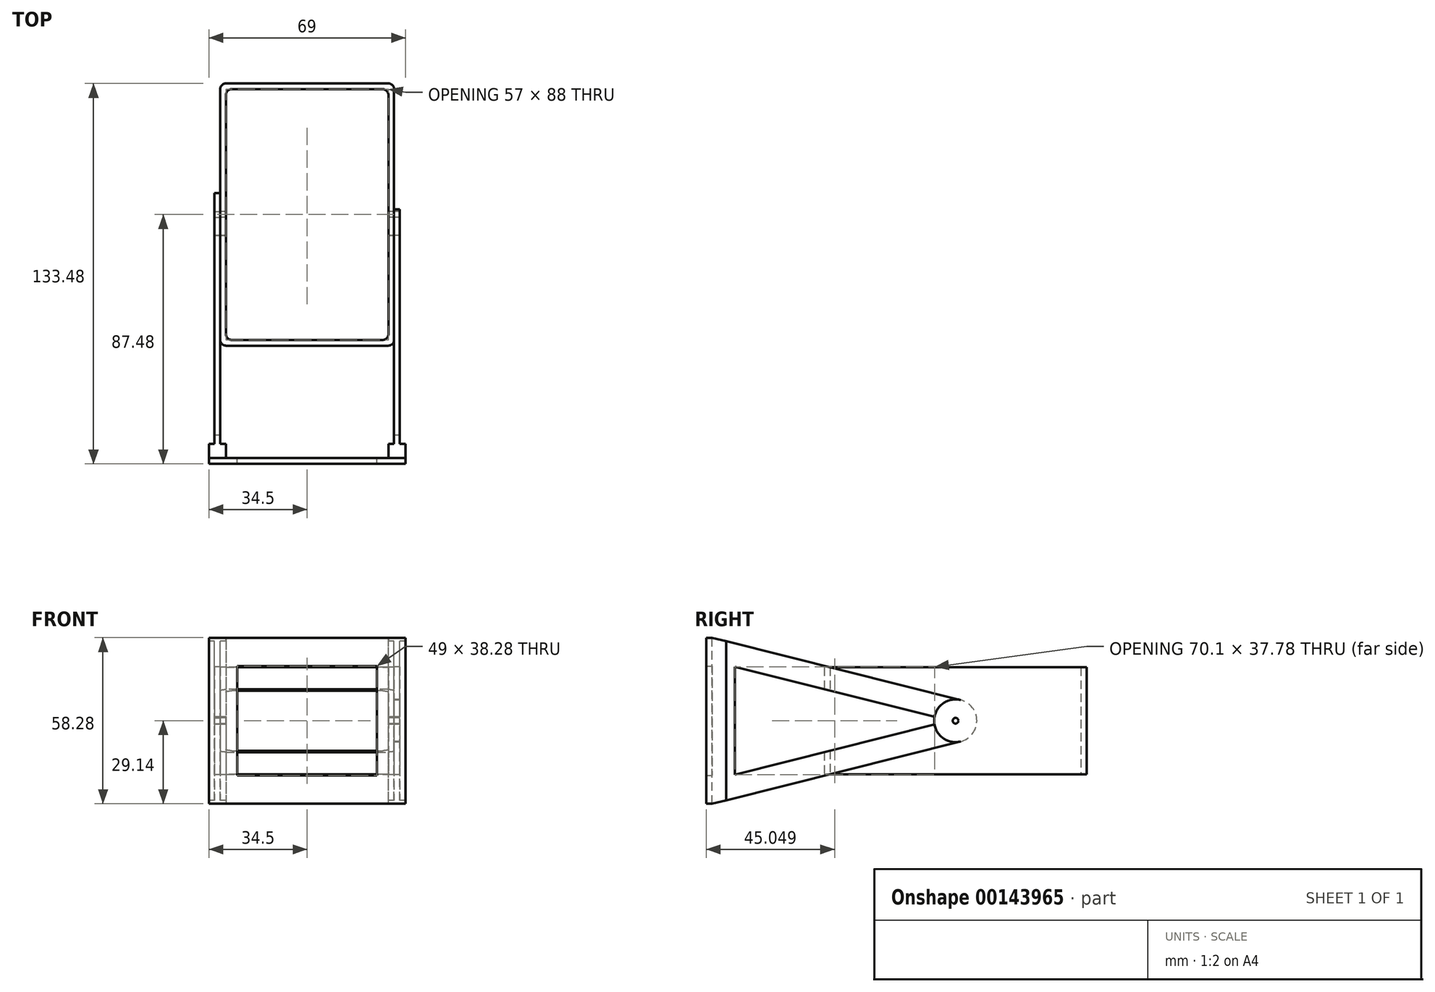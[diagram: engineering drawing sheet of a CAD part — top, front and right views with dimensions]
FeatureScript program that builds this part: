
annotation { "Feature Type Name" : "Feature", "Feature Type Description" : "" }
export const myFeature = defineFeature(function(context is Context, id is Id, definition is map)
    precondition{}
    {
        {
            var Q0;
            Q0=qCreatedBy(makeId("Top.planeOp"),FACE);
            var sketch = newSketch(context, id + "F0", { "sketchPlane" : qUnion([Q0])});
            skLineSegment(sketch, "E0", {"start": v(-28.5, 0) * mm, "end": v(-28.5, 42) * mm});
            skLineSegment(sketch, "E1", {"start": v(-26.5, 44) * mm, "end": v(26.5, 44) * mm});
            skLineSegment(sketch, "E2", {"start": v(28.5, 42) * mm, "end": v(28.5, 0) * mm});
            skLineSegment(sketch, "E3", {"start": v(28.5, 0) * mm, "end": v(28.5, -42) * mm});
            skLineSegment(sketch, "E4", {"start": v(26.5, -44) * mm, "end": v(-26.5, -44) * mm});
            skLineSegment(sketch, "E5", {"start": v(-28.5, -42) * mm, "end": v(-28.5, 0) * mm});
            skLineSegment(sketch, "E6", {"start": v(0, 0) * mm, "end": v(28.5, 0) * mm, "construction": true});
            skLineSegment(sketch, "E7", {"start": v(0, 0) * mm, "end": v(-28.5, 0) * mm, "construction": true});
            skPoint(sketch, "E8.visualSharp", {"position": v(-28.5, 44) * mm});
            skArc(sketch, "E8.filletArc", {"start": v(-26.5, 44) * mm, "mid": v(-27.91, 43.41) * mm, "end": v(-28.5, 42) * mm});
            skPoint(sketch, "E9.visualSharp", {"position": v(28.5, 44) * mm});
            skArc(sketch, "E9.filletArc", {"start": v(28.5, 42) * mm, "mid": v(27.91, 43.41) * mm, "end": v(26.5, 44) * mm});
            skPoint(sketch, "E10.visualSharp", {"position": v(28.5, -44) * mm});
            skArc(sketch, "E10.filletArc", {"start": v(26.5, -44) * mm, "mid": v(27.91, -43.41) * mm, "end": v(28.5, -42) * mm});
            skPoint(sketch, "E11.visualSharp", {"position": v(-28.5, -44) * mm});
            skArc(sketch, "E11.filletArc", {"start": v(-28.5, -42) * mm, "mid": v(-27.91, -43.41) * mm, "end": v(-26.5, -44) * mm});
            skLineSegment(sketch, "E12", {"start": v(-30.5, 0) * mm, "end": v(-30.5, 44) * mm});
            skLineSegment(sketch, "E13", {"start": v(-28.5, 46) * mm, "end": v(28.5, 46) * mm});
            skLineSegment(sketch, "E14", {"start": v(30.5, 44) * mm, "end": v(30.5, 0) * mm});
            skLineSegment(sketch, "E15", {"start": v(30.5, 0) * mm, "end": v(30.5, -44) * mm});
            skLineSegment(sketch, "E16", {"start": v(28.5, -46) * mm, "end": v(-28.5, -46) * mm});
            skLineSegment(sketch, "E17", {"start": v(-30.5, -44) * mm, "end": v(-30.5, 0) * mm});
            skPoint(sketch, "E18.visualSharp", {"position": v(-30.5, 46) * mm});
            skArc(sketch, "E18.filletArc", {"start": v(-28.5, 46) * mm, "mid": v(-29.91, 45.41) * mm, "end": v(-30.5, 44) * mm});
            skPoint(sketch, "E19.visualSharp", {"position": v(30.5, 46) * mm});
            skArc(sketch, "E19.filletArc", {"start": v(30.5, 44) * mm, "mid": v(29.91, 45.41) * mm, "end": v(28.5, 46) * mm});
            skPoint(sketch, "E20.visualSharp", {"position": v(30.5, -46) * mm});
            skArc(sketch, "E20.filletArc", {"start": v(28.5, -46) * mm, "mid": v(29.91, -45.41) * mm, "end": v(30.5, -44) * mm});
            skPoint(sketch, "E21.visualSharp", {"position": v(-30.5, -46) * mm});
            skArc(sketch, "E21.filletArc", {"start": v(-30.5, -44) * mm, "mid": v(-29.91, -45.41) * mm, "end": v(-28.5, -46) * mm});
            skLineSegment(sketch, "E22", {"start": v(0, 0) * mm, "end": v(0, -46) * mm, "construction": true});
            skLineSegment(sketch, "E23", {"start": v(10, -44) * mm, "end": v(10, -29) * mm});
            skLineSegment(sketch, "E24", {"start": v(-10, -29) * mm, "end": v(-10, -44) * mm});
            skLineSegment(sketch, "E25", {"start": v(-8, -27) * mm, "end": v(0, -27) * mm});
            skLineSegment(sketch, "E26", {"start": v(0, -27) * mm, "end": v(8, -27) * mm});
            skPoint(sketch, "E27.visualSharp", {"position": v(10, -27) * mm});
            skArc(sketch, "E27.filletArc", {"start": v(10, -29) * mm, "mid": v(9.41, -27.59) * mm, "end": v(8, -27) * mm});
            skPoint(sketch, "E28.visualSharp", {"position": v(-10, -27) * mm});
            skArc(sketch, "E28.filletArc", {"start": v(-8, -27) * mm, "mid": v(-9.41, -27.59) * mm, "end": v(-10, -29) * mm});
            skLineSegment(sketch, "E29", {"start": v(9.5, -44) * mm, "end": v(9.5, -41) * mm});
            skLineSegment(sketch, "E30", {"start": v(9.2, -40.7) * mm, "end": v(0, -40.7) * mm});
            skLineSegment(sketch, "E31", {"start": v(0, -40.7) * mm, "end": v(-5.2, -40.7) * mm});
            skLineSegment(sketch, "E32", {"start": v(-5.5, -41) * mm, "end": v(-5.5, -44) * mm});
            skPoint(sketch, "E33.visualSharp", {"position": v(9.5, -40.7) * mm});
            skArc(sketch, "E33.filletArc", {"start": v(9.5, -41) * mm, "mid": v(9.41, -40.79) * mm, "end": v(9.2, -40.7) * mm});
            skPoint(sketch, "E34.visualSharp", {"position": v(-5.5, -40.7) * mm});
            skArc(sketch, "E34.filletArc", {"start": v(-5.2, -40.7) * mm, "mid": v(-5.41, -40.79) * mm, "end": v(-5.5, -41) * mm});
            skPoint(sketch, "E35.cornerSnap0", {"position": v(-29.91, -45.41) * mm});
            skSolve(sketch);
        }
        {
            var Q0;
            Q0=makeQuery(id+"F0.imprint","IMPRINT",FACE,{"disambiguationData":[TD([[makeQuery(id+"F0.imprint","IMPRINT",EDGE,{"derivedFrom":sQuery(id+"F0.wireOp",EDGE,"E0")}),1.0]])]});
            extrude(context, id + "F1", {"entities" : qUnion([Q0]), "depth" : 35 * mm, "hasSecondDirection" : true, "secondDirectionOppositeDirection" : true, "secondDirectionDepth" : 2.5 * mm});
        }
        {
            var Q0;
            Q0=makeQuery(id+"F1.opExtrude","SWEPT_FACE",FACE,{"disambiguationData":[OSD([sQuery(id+"F0.wireOp",EDGE,"E12"),sQuery(id+"F0.wireOp",EDGE,"E17")])]});
            var sketch = newSketch(context, id + "F2", { "sketchPlane" : qUnion([Q0])});
            skCircle(sketch, "E36", {"center": v(0, 16.25) * mm, "radius": 1 * mm});
            skLineSegment(sketch, "E37.0", {"start": v(-44, 35) * mm, "end": v(-44, -2.5) * mm});
            skLineSegment(sketch, "E38.0", {"start": v(44, 35) * mm, "end": v(44, -2.5) * mm});
            skLineSegment(sketch, "E39", {"start": v(44, -2.5) * mm, "end": v(-44, 35) * mm, "construction": true});
            skLineSegment(sketch, "E40", {"start": v(-44, -2.5) * mm, "end": v(44, 35) * mm, "construction": true});
            skSolve(sketch);
        }
        {
            var Q0;
            Q0=makeQuery(id+"F2.imprint","IMPRINT",FACE,{"disambiguationData":[TD([[makeQuery(id+"F2.imprint","IMPRINT",EDGE,{"derivedFrom":sQuery(id+"F2.wireOp",EDGE,"E36")}),1.0]])]});
            extrude(context, id + "F3", {"entities" : qUnion([Q0]), "operationType" : NewBodyOperationType.REMOVE, "endBound" : BoundingType.THROUGH_ALL, "oppositeDirection" : true, "depth" : 25 * mm});
        }
        {
            var Q0;
            Q0=makeQuery(id+"F1.opExtrude","SWEPT_FACE",FACE,{"disambiguationData":[OSD([sQuery(id+"F0.wireOp",EDGE,"E12"),sQuery(id+"F0.wireOp",EDGE,"E17")])]});
            cPlane(context, id + "F4", {"entities" : qUnion([Q0]), "cplaneType" : CPlaneType.OFFSET, "offset" : 0 * mm, "width" : 150 * mm, "height" : 150 * mm});
        }
        {
            var Q0;
            Q0=qCreatedBy(id+"F4.planeOp",FACE);
            var sketch = newSketch(context, id + "F5", { "sketchPlane" : qUnion([Q0])});
            skCircle(sketch, "E41.0", {"center": v(0, 16.25) * mm, "radius": 1 * mm});
            skCircle(sketch, "E42", {"center": v(0, 16.25) * mm, "radius": 7.5 * mm});
            skLineSegment(sketch, "E43.0", {"start": v(44, 35) * mm, "end": v(44, -2.5) * mm});
            skLineSegment(sketch, "E44", {"start": v(-1.82, 8.97) * mm, "end": v(85.48, -12.89) * mm});
            skLineSegment(sketch, "E45", {"start": v(-1.82, 23.53) * mm, "end": v(85.48, 45.39) * mm});
            skLineSegment(sketch, "E46", {"start": v(85.48, -12.89) * mm, "end": v(85.48, 45.39) * mm});
            skSolve(sketch);
        }
        {
            var Q0;
            {var subQ0=sQuery(id+"F5.wireOp",EDGE,"E43.0");Q0=makeQuery(id+"F5.imprint","IMPRINT",FACE,{"disambiguationData":[TD([[makeQuery(id+"F5.imprint","IMPRINT",EDGE,{"derivedFrom":subQ0}),1.0]])]});}
            var Q1;
            {var subQ5=sQuery(id+"F5.wireOp",EDGE,"E43.0");Q1=makeQuery(id+"F5.imprint","IMPRINT",FACE,{"disambiguationData":[TD([[makeQuery(id+"F5.imprint","IMPRINT",EDGE,{"derivedFrom":subQ5}),-1.0]])]});}
            var Q2;
            Q2=makeQuery(id+"F5.imprint","IMPRINT",FACE,{"disambiguationData":[TD([[makeQuery(id+"F5.imprint","IMPRINT",EDGE,{"derivedFrom":sQuery(id+"F5.wireOp",EDGE,"E41.0")}),-1.0]])]});
            extrude(context, id + "F6", {"entities" : qUnion([Q0, Q1, Q2]), "depth" : 2 * mm});
        }
        {
            var Q0;
            Q0=makeQuery(id+"F1.opExtrude","SWEPT_FACE",FACE,{"disambiguationData":[OSD([sQuery(id+"F0.wireOp",EDGE,"E14"),sQuery(id+"F0.wireOp",EDGE,"E15")])]});
            cPlane(context, id + "F7", {"entities" : qUnion([Q0]), "cplaneType" : CPlaneType.OFFSET, "offset" : 0 * mm, "width" : 150 * mm, "height" : 150 * mm});
        }
        {
            var Q0;
            Q0=qCreatedBy(id+"F7.planeOp",FACE);
            var sketch = newSketch(context, id + "F8", { "sketchPlane" : qUnion([Q0])});
            skLineSegment(sketch, "E47.0", {"start": v(1.82, 23.53) * mm, "end": v(-85.48, 45.39) * mm});
            skCircle(sketch, "E47.1", {"center": v(0, 16.25) * mm, "radius": 7.5 * mm});
            skCircle(sketch, "E47.2", {"center": v(0, 16.25) * mm, "radius": 1 * mm});
            skLineSegment(sketch, "E47.3", {"start": v(1.82, 8.97) * mm, "end": v(-85.48, -12.89) * mm});
            skLineSegment(sketch, "E47.4", {"start": v(-85.48, -12.89) * mm, "end": v(-85.48, 45.39) * mm});
            skSolve(sketch);
        }
        {
            var Q0;
            {var subQ0=sQuery(id+"F8.wireOp",EDGE,"E47.0");Q0=makeQuery(id+"F8.imprint","IMPRINT",FACE,{"disambiguationData":[TD([[makeQuery(id+"F8.imprint","IMPRINT",EDGE,{"derivedFrom":subQ0}),1.0]])]});}
            var Q1;
            Q1=makeQuery(id+"F8.imprint","IMPRINT",FACE,{"disambiguationData":[TD([[makeQuery(id+"F8.imprint","IMPRINT",EDGE,{"derivedFrom":sQuery(id+"F8.wireOp",EDGE,"E47.2")}),1.0]])]});
            extrude(context, id + "F9", {"entities" : qUnion([Q0, Q1]), "depth" : 2 * mm});
        }
        {
            var Q0;
            Q0=makeQuery(id+"F6.opExtrude","SWEPT_FACE",FACE,{"disambiguationData":[OSD([sQuery(id+"F5.wireOp",EDGE,"E46")])]});
            var sketch = newSketch(context, id + "F10", { "sketchPlane" : qUnion([Q0])});
            skLineSegment(sketch, "E48.0", {"start": v(32.5, -12.89) * mm, "end": v(32.5, 45.39) * mm});
            skLineSegment(sketch, "E48.1", {"start": v(30.5, -12.89) * mm, "end": v(30.5, 45.39) * mm});
            skLineSegment(sketch, "E48.2", {"start": v(-30.5, -12.89) * mm, "end": v(-30.5, 45.39) * mm});
            skLineSegment(sketch, "E48.3", {"start": v(-32.5, -12.89) * mm, "end": v(-32.5, 45.39) * mm});
            skLineSegment(sketch, "E49", {"start": v(34.5, -12.89) * mm, "end": v(-34.5, -12.89) * mm});
            skPoint(sketch, "E49.endSnap0", {"position": v(-31.5, -12.89) * mm});
            skLineSegment(sketch, "E50", {"start": v(-34.5, -12.89) * mm, "end": v(-34.5, 45.39) * mm});
            skLineSegment(sketch, "E51", {"start": v(-34.5, 45.39) * mm, "end": v(34.5, 45.39) * mm});
            skLineSegment(sketch, "E52", {"start": v(34.5, 45.39) * mm, "end": v(34.5, -12.89) * mm});
            skLineSegment(sketch, "E53", {"start": v(28.5, -12.89) * mm, "end": v(28.5, 45.39) * mm});
            skLineSegment(sketch, "E54", {"start": v(-28.5, 45.39) * mm, "end": v(-28.5, -12.89) * mm});
            skLineSegment(sketch, "E55.bottom", {"start": v(-24.5, 35.39) * mm, "end": v(24.5, 35.39) * mm});
            skLineSegment(sketch, "E55.top", {"start": v(-24.5, -2.89) * mm, "end": v(24.5, -2.89) * mm});
            skLineSegment(sketch, "E55.left", {"start": v(-24.5, 35.39) * mm, "end": v(-24.5, -2.89) * mm});
            skLineSegment(sketch, "E55.right", {"start": v(24.5, 35.39) * mm, "end": v(24.5, -2.89) * mm});
            skSolve(sketch);
        }
        {
            var Q0;
            {var subQ0=sQuery(id+"F10.wireOp",EDGE,"E48.0");Q0=makeQuery(id+"F10.imprint","IMPRINT",FACE,{"disambiguationData":[TD([[makeQuery(id+"F10.imprint","IMPRINT",EDGE,{"derivedFrom":subQ0}),-1.0]])]});}
            var Q1;
            {var subQ0=sQuery(id+"F10.wireOp",EDGE,"E48.1");Q1=makeQuery(id+"F10.imprint","IMPRINT",FACE,{"disambiguationData":[TD([[makeQuery(id+"F10.imprint","IMPRINT",EDGE,{"derivedFrom":subQ0}),1.0]])]});}
            var Q2;
            {var subQ0=sQuery(id+"F10.wireOp",EDGE,"E48.2");Q2=makeQuery(id+"F10.imprint","IMPRINT",FACE,{"disambiguationData":[TD([[makeQuery(id+"F10.imprint","IMPRINT",EDGE,{"derivedFrom":subQ0}),-1.0]])]});}
            var Q3;
            {var subQ0=sQuery(id+"F10.wireOp",EDGE,"E48.3");Q3=makeQuery(id+"F10.imprint","IMPRINT",FACE,{"disambiguationData":[TD([[makeQuery(id+"F10.imprint","IMPRINT",EDGE,{"derivedFrom":subQ0}),1.0]])]});}
            extrude(context, id + "F11", {"entities" : qUnion([Q0, Q1, Q2, Q3]), "oppositeDirection" : true, "depth" : 5 * mm});
        }
        {
            var Q0;
            {var subQ0=sQuery(id+"F10.wireOp",EDGE,"E48.0");Q0=makeQuery(id+"F10.imprint","IMPRINT",FACE,{"disambiguationData":[TD([[makeQuery(id+"F10.imprint","IMPRINT",EDGE,{"derivedFrom":subQ0}),-1.0]])]});}
            var Q1;
            {var subQ0=sQuery(id+"F10.wireOp",EDGE,"E48.0");Q1=makeQuery(id+"F10.imprint","IMPRINT",FACE,{"disambiguationData":[TD([[makeQuery(id+"F10.imprint","IMPRINT",EDGE,{"derivedFrom":subQ0}),1.0]])]});}
            var Q2;
            {var subQ0=sQuery(id+"F10.wireOp",EDGE,"E53");Q2=makeQuery(id+"F10.imprint","IMPRINT",FACE,{"disambiguationData":[TD([[makeQuery(id+"F10.imprint","IMPRINT",EDGE,{"derivedFrom":subQ0}),1.0]])]});}
            var Q3;
            {var subQ0=sQuery(id+"F10.wireOp",EDGE,"E48.2");Q3=makeQuery(id+"F10.imprint","IMPRINT",FACE,{"disambiguationData":[TD([[makeQuery(id+"F10.imprint","IMPRINT",EDGE,{"derivedFrom":subQ0}),-1.0]])]});}
            var Q4;
            {var subQ0=sQuery(id+"F10.wireOp",EDGE,"E48.2");Q4=makeQuery(id+"F10.imprint","IMPRINT",FACE,{"disambiguationData":[TD([[makeQuery(id+"F10.imprint","IMPRINT",EDGE,{"derivedFrom":subQ0}),1.0]])]});}
            var Q5;
            {var subQ0=sQuery(id+"F10.wireOp",EDGE,"E48.3");Q5=makeQuery(id+"F10.imprint","IMPRINT",FACE,{"disambiguationData":[TD([[makeQuery(id+"F10.imprint","IMPRINT",EDGE,{"derivedFrom":subQ0}),1.0]])]});}
            var Q6;
            {var subQ0=sQuery(id+"F10.wireOp",EDGE,"E48.1");Q6=makeQuery(id+"F10.imprint","IMPRINT",FACE,{"disambiguationData":[TD([[makeQuery(id+"F10.imprint","IMPRINT",EDGE,{"derivedFrom":subQ0}),1.0]])]});}
            extrude(context, id + "F12", {"entities" : qUnion([Q0, Q1, Q2, Q3, Q4, Q5, Q6]), "operationType" : NewBodyOperationType.ADD, "depth" : 2 * mm});
        }
        {
            var Q0;
            {var subQ0=sQuery(id+"F10.wireOp",EDGE,"E50");Q0=makeQuery(id+"F12.boolean.opBoolean","MERGE",FACE,{"derivedFrom":[makeQuery(id+"F11.opExtrude","SWEPT_FACE",FACE,{"disambiguationData":[OSD([subQ0])]}),makeQuery(id+"F12.opExtrude","SWEPT_FACE",FACE,{"disambiguationData":[OSD([subQ0])]})]});}
            var sketch = newSketch(context, id + "F13", { "sketchPlane" : qUnion([Q0])});
            skLineSegment(sketch, "E56.0", {"start": v(-1.82, 23.53) * mm, "end": v(85.48, 45.39) * mm});
            skLineSegment(sketch, "E57.0", {"start": v(-1.82, 8.97) * mm, "end": v(85.48, -12.89) * mm});
            skSolve(sketch);
        }
        {
            var Q0;
            {var subQ0=sQuery(id+"F13.wireOp",EDGE,"E57.0");var subQ1=sQuery(id+"F10.wireOp",EDGE,"E50");var subQ5=makeQuery(id+"F11.opExtrude","CAP_EDGE",EDGE,{"disambiguationData":[OSD([subQ1])],"isStart":false});var subQ6=makeQuery(id+"F13.imprint","INTERSECT",VERTEX,{"derivedFrom":[subQ5,subQ0]});Q0=makeQuery(id+"F13.imprint","IMPRINT",FACE,{"disambiguationData":[TD([[makeQuery(id+"F13.imprint","IMPRINT",EDGE,{"disambiguationData":[TD([[subQ6,-1.0]])],"derivedFrom":subQ0}),-1.0]])]});}
            var Q1;
            {var subQ0=sQuery(id+"F13.wireOp",EDGE,"E56.0");var subQ2=sQuery(id+"F10.wireOp",EDGE,"E50");var subQ5=makeQuery(id+"F11.opExtrude","CAP_EDGE",EDGE,{"disambiguationData":[OSD([subQ2])],"isStart":false});var subQ6=makeQuery(id+"F13.imprint","INTERSECT",VERTEX,{"derivedFrom":[subQ5,subQ0]});Q1=makeQuery(id+"F13.imprint","IMPRINT",FACE,{"disambiguationData":[TD([[makeQuery(id+"F13.imprint","IMPRINT",EDGE,{"disambiguationData":[TD([[subQ6,-1.0]])],"derivedFrom":subQ0}),1.0]])]});}
            extrude(context, id + "F14", {"entities" : qUnion([Q0, Q1]), "operationType" : NewBodyOperationType.REMOVE, "endBound" : BoundingType.THROUGH_ALL, "oppositeDirection" : true, "depth" : 25 * mm});
        }
        {
            var Q0;
            Q0=makeQuery(id+"F6.opExtrude","CAP_FACE",FACE,{"disambiguationData":[OSD([sQuery(id+"F5.wireOp",EDGE,"E41.0"),sQuery(id+"F5.wireOp",EDGE,"E42"),sQuery(id+"F5.wireOp",EDGE,"E44"),sQuery(id+"F5.wireOp",EDGE,"E45"),sQuery(id+"F5.wireOp",EDGE,"E46")])],"isStart":false});
            var sketch = newSketch(context, id + "F15", { "sketchPlane" : qUnion([Q0])});
            skCircle(sketch, "E58.0", {"center": v(0, 16.25) * mm, "radius": 7.5 * mm});
            skLineSegment(sketch, "E59.0", {"start": v(-1.82, 8.97) * mm, "end": v(85.48, -12.89) * mm});
            skLineSegment(sketch, "E60.0", {"start": v(-1.82, 23.53) * mm, "end": v(85.48, 45.39) * mm});
            skLineSegment(sketch, "E61", {"start": v(7.38, 14.92) * mm, "end": v(77.48, -2.64) * mm});
            skLineSegment(sketch, "E62", {"start": v(77.48, -2.64) * mm, "end": v(77.48, 35.14) * mm});
            skLineSegment(sketch, "E63", {"start": v(77.48, 35.14) * mm, "end": v(7.38, 17.58) * mm});
            skSolve(sketch);
        }
        {
            var Q0;
            {var subQ0=sQuery(id+"F15.wireOp",EDGE,"E61");Q0=makeQuery(id+"F15.imprint","IMPRINT",FACE,{"disambiguationData":[TD([[makeQuery(id+"F15.imprint","IMPRINT",EDGE,{"derivedFrom":subQ0}),1.0]])]});}
            extrude(context, id + "F16", {"entities" : qUnion([Q0]), "operationType" : NewBodyOperationType.REMOVE, "endBound" : BoundingType.THROUGH_ALL, "oppositeDirection" : true, "depth" : 25 * mm});
        }
    });
